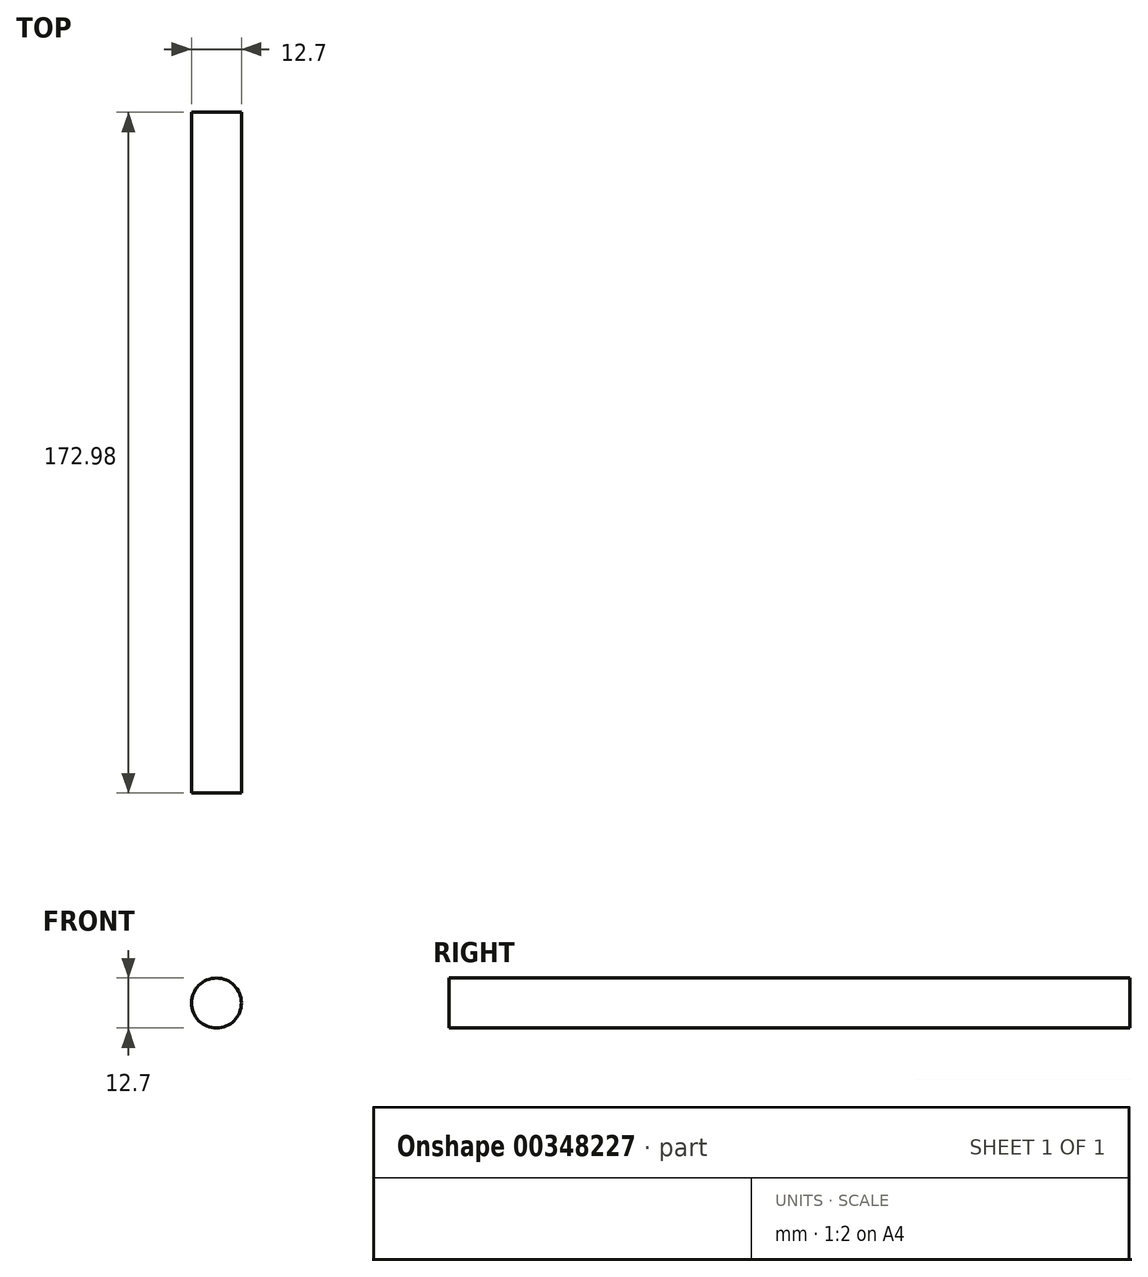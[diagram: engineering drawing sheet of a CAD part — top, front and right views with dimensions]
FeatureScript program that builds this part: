
annotation { "Feature Type Name" : "Feature", "Feature Type Description" : "" }
export const myFeature = defineFeature(function(context is Context, id is Id, definition is map)
    precondition{}
    {
        {
            var Q0;
            Q0=qCreatedBy(makeId("Front.planeOp"),FACE);
            var sketch = newSketch(context, id + "F0", { "sketchPlane" : qUnion([Q0])});
            skCircle(sketch, "E0", {"center": v(0, 0) * mm, "radius": 6.35 * mm});
            skSolve(sketch);
        }
        {
            var Q0;
            Q0=qSketchRegion(id+"F0",true);
            extrude(context, id + "F1", {"entities" : qUnion([Q0]), "endBound" : BoundingType.SYMMETRIC, "depth" : 172.97 * mm});
        }
    });
